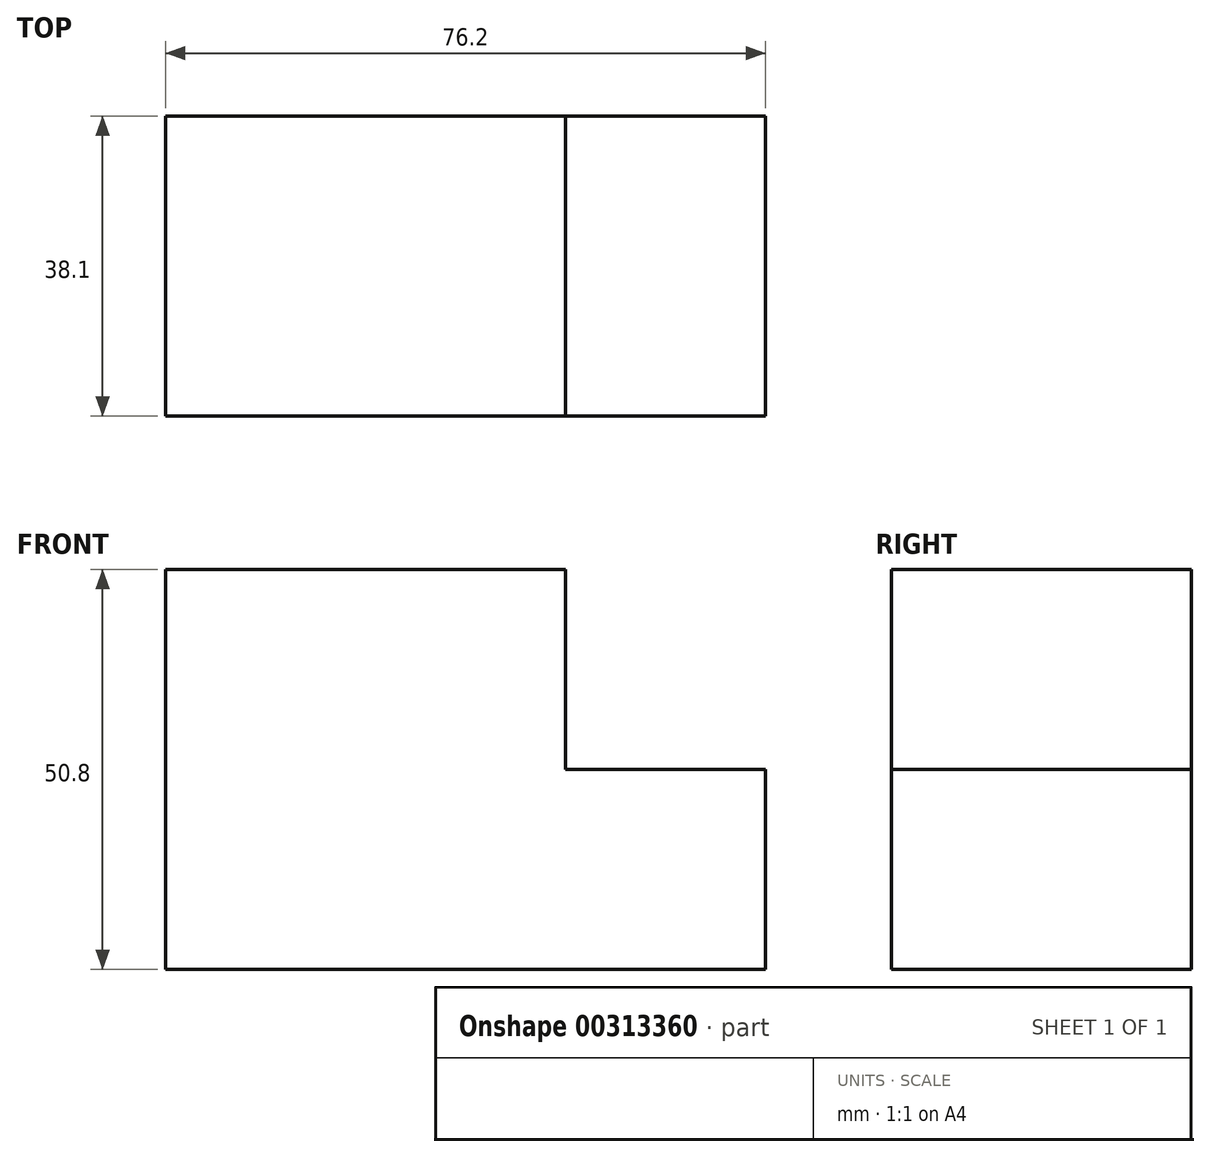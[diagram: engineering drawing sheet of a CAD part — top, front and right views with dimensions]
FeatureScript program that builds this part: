
annotation { "Feature Type Name" : "Feature", "Feature Type Description" : "" }
export const myFeature = defineFeature(function(context is Context, id is Id, definition is map)
    precondition{}
    {
        {
            var Q0;
            Q0=qCreatedBy(makeId("Front.planeOp"),FACE);
            var sketch = newSketch(context, id + "F0", { "sketchPlane" : qUnion([Q0])});
            skLineSegment(sketch, "E0", {"start": v(-38.87, -39.46) * mm, "end": v(37.33, -39.46) * mm});
            skLineSegment(sketch, "E1", {"start": v(37.33, -39.46) * mm, "end": v(37.33, -14.06) * mm});
            skLineSegment(sketch, "E2", {"start": v(37.33, -14.06) * mm, "end": v(11.93, -14.06) * mm});
            skLineSegment(sketch, "E3", {"start": v(11.93, -14.06) * mm, "end": v(11.93, 11.34) * mm});
            skLineSegment(sketch, "E4", {"start": v(11.93, 11.34) * mm, "end": v(-38.87, 11.34) * mm});
            skLineSegment(sketch, "E5", {"start": v(-38.87, 11.34) * mm, "end": v(-38.87, -39.46) * mm});
            skSolve(sketch);
        }
        {
            var Q0;
            Q0=makeQuery(id+"F0.imprint","IMPRINT",FACE,{"disambiguationData":[TD([[makeQuery(id+"F0.imprint","IMPRINT",EDGE,{"derivedFrom":sQuery(id+"F0.wireOp",EDGE,"E0")}),1.0]])]});
            extrude(context, id + "F1", {"entities" : qUnion([Q0]), "depth" : 38.1 * mm});
        }
    });
